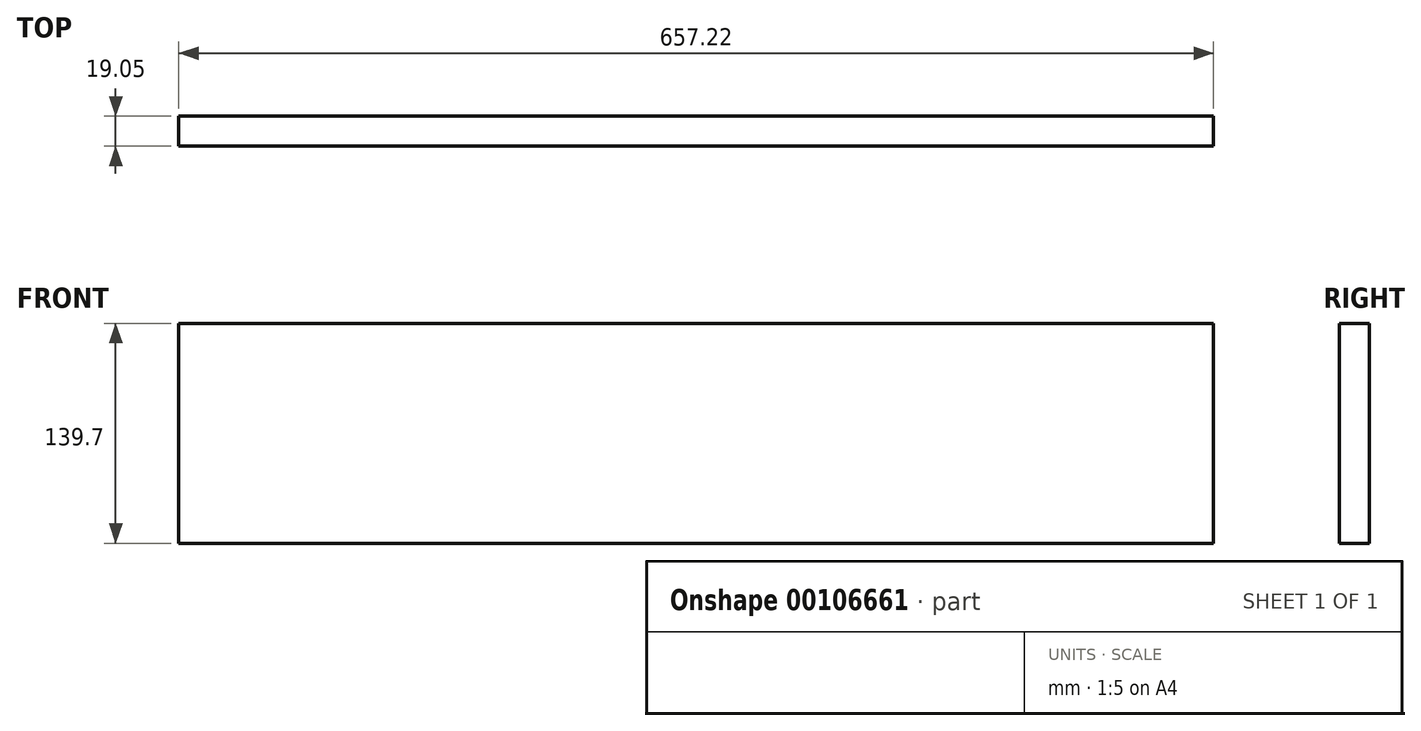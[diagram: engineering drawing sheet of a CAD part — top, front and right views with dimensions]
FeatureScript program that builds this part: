
annotation { "Feature Type Name" : "Feature", "Feature Type Description" : "" }
export const myFeature = defineFeature(function(context is Context, id is Id, definition is map)
    precondition{}
    {
        {
            var Q0;
            Q0=qCreatedBy(makeId("Front.planeOp"),FACE);
            var sketch = newSketch(context, id + "F0", { "sketchPlane" : qUnion([Q0])});
            skLineSegment(sketch, "E0.bottom", {"start": v(0, 0) * mm, "end": v(657.23, 0) * mm});
            skLineSegment(sketch, "E0.top", {"start": v(0, 139.7) * mm, "end": v(657.23, 139.7) * mm});
            skLineSegment(sketch, "E0.left", {"start": v(0, 0) * mm, "end": v(0, 139.7) * mm});
            skLineSegment(sketch, "E0.right", {"start": v(657.23, 0) * mm, "end": v(657.23, 139.7) * mm});
            skSolve(sketch);
        }
        {
            var Q0;
            Q0=makeQuery(id+"F0.imprint","IMPRINT",FACE,{"disambiguationData":[TD([[makeQuery(id+"F0.imprint","IMPRINT",EDGE,{"derivedFrom":sQuery(id+"F0.wireOp",EDGE,"E0.bottom")}),1.0]])]});
            extrude(context, id + "F1", {"entities" : qUnion([Q0]), "depth" : 19.05 * mm});
        }
    });
